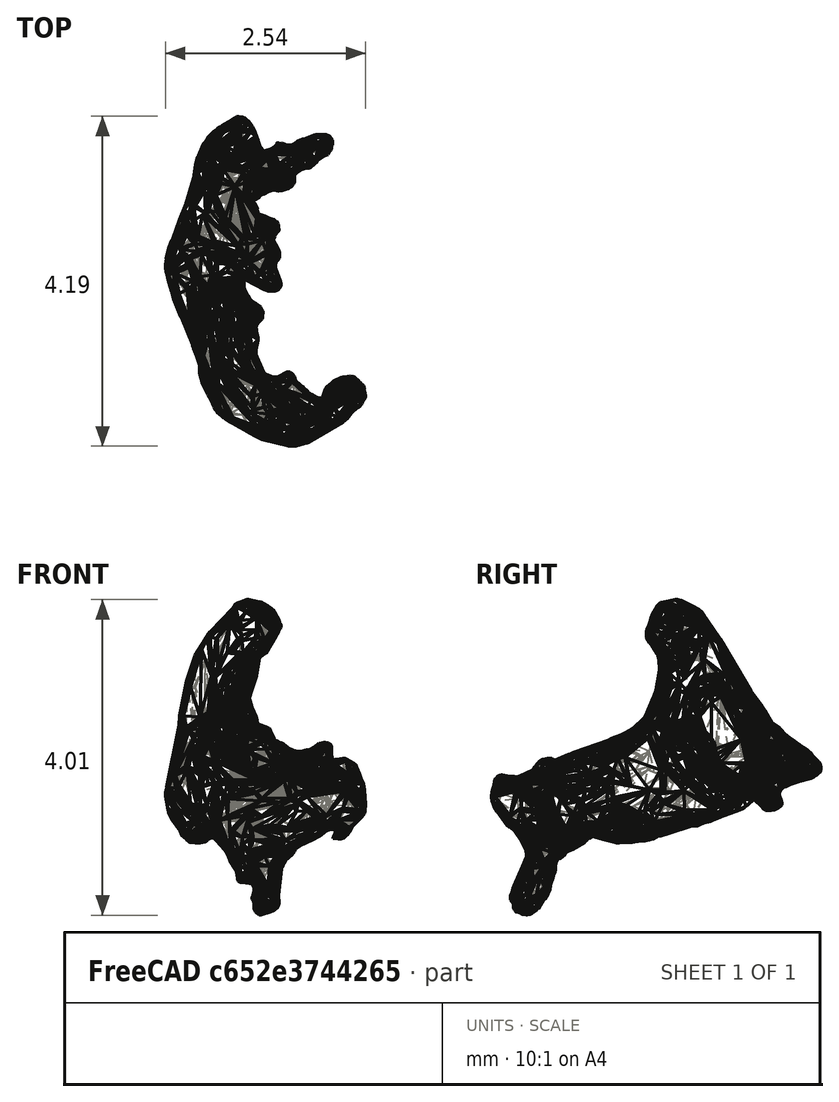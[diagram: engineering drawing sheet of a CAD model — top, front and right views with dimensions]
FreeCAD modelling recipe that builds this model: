
FCSTD DOCUMENT  (FreeCAD 0.20R29603 (Git))
Label: ii_sclerite
License: All rights reserved
LicenseURL: http://en.wikipedia.org/wiki/All_rights_reserved
objects: Mesh::Feature×4, Part::Feature×1, PartDesign::FeatureBase×1, PartDesign::Plane×1, Sketcher::SketchObject×1, PartDesign::Point×1, PartDesign::Line×1, PartDesign::Body×1
note: 7 computed .brp shape members not serialized (recipe doc carries the construction recipe); baked Part::Feature solids carry a one-line shape summary decoded from their .brp

FEATURE [Mesh::Feature] ii_sclerite
FEATURE [Part::Feature] ii_sclerite001
  shape: bbox 2.539 x 4.186 x 4.011 mm, 10226 faces, 0 solids (baked)
FEATURE [PartDesign::FeatureBase] BaseFeature
  BaseFeature = -> ii_sclerite001
FEATURE [Mesh::Feature] i_sclerite
FEATURE [PartDesign::Plane] DatumPlane  label="i_sclerite_axis_DatumPlane"
  AttachmentOffset = pos=(0,0,5.3) rot=(-1,0,0;0.244346rad)
  Length = 61.0101
  MapMode = 5
  Placement = pos=(0,0,5.3) rot=(-1,0,0;0.244346rad)
  ResizeMode = 0
  Support = -> [XY_Plane]
  Width = 71.621
FEATURE [Mesh::Feature] pwp
FEATURE [Mesh::Feature] sla
FEATURE [Sketcher::SketchObject] Sketch  label="i_sclerite_axis_Sketch"
  FullyConstrained = true
  MapMode = 5
  Placement = pos=(0,0,5.3) rot=(-1,0,0;0.244346rad)
  Support = -> [DatumPlane]
  sketch-geometry (2):
    g0: LineSegment StartX=-2.30726 StartY=5.95982 StartZ=0 EndX=1.5 EndY=0 EndZ=0
    g1: GeomPoint X=-0.544487 Y=3.20041 Z=0
  constraints (6):
    c: PointOnObject(g0,g-1)
    c: Distance(g0) = 7.0721
    c: Angle(g0,g-1) = 1.00232
    c: DistanceX(g-1,g0) = 1.5
    c: PointOnObject(g1,g0)
    c: Distance(g1,g0) = 3.7977
FEATURE [PartDesign::Point] DatumPoint  label="i_sclerite_axis_DatumPoint"
  AttacherType = Attacher::AttachEnginePoint
  MapMode = 37
  Placement = pos=(-0.544487,3.10534,4.52575) rot=(0,0,1;0rad)
  Support = -> [Sketch]
FEATURE [PartDesign::Line] DatumLine  label="i_sclerite_axis_DatumLine"
  AttacherType = Attacher::AttachEngineLine
  Length = 20
  MapMode = 29
  Placement = pos=(1.06527,0.660303,5.13537) rot=(0.903308,0.270662,0.332833;1.46591rad)
  ResizeMode = 0
  Support = -> [Sketch]
FEATURE [PartDesign::Body] Body  label="ii_sclerite_Body"
  BaseFeature = -> ii_sclerite001
  Group = -> [BaseFeature,DatumPlane,Sketch,DatumPoint,DatumLine]
  Origin = -> Origin
  Tip = -> BaseFeature
